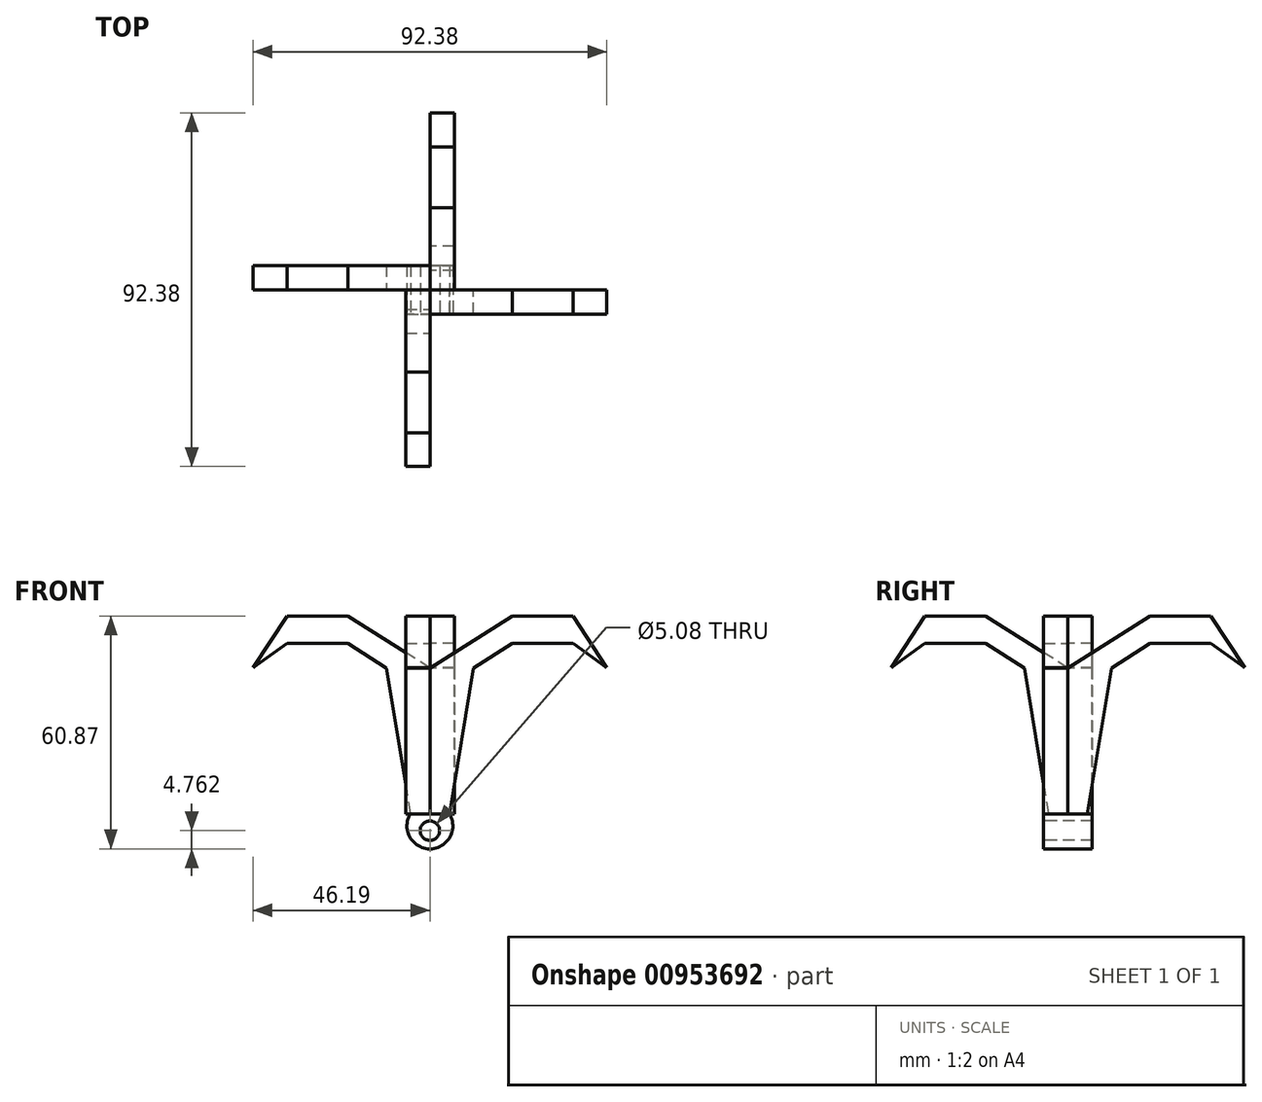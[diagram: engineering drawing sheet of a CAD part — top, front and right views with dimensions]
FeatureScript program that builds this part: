
annotation { "Feature Type Name" : "Feature", "Feature Type Description" : "" }
export const myFeature = defineFeature(function(context is Context, id is Id, definition is map)
    precondition{}
    {
        {
            var Q0;
            Q0=qCreatedBy(makeId("Front.planeOp"),FACE);
            var sketch = newSketch(context, id + "F0", { "sketchPlane" : qUnion([Q0])});
            skLineSegment(sketch, "E0", {"start": v(0, 0) * mm, "end": v(0, 38.1) * mm});
            skLineSegment(sketch, "E1", {"start": v(0, 38.1) * mm, "end": v(21.45, 51.7) * mm});
            skLineSegment(sketch, "E2", {"start": v(21.45, 51.7) * mm, "end": v(37.33, 51.7) * mm});
            skLineSegment(sketch, "E3", {"start": v(37.33, 51.7) * mm, "end": v(46.19, 38.2) * mm});
            skLineSegment(sketch, "E4", {"start": v(46.19, 38.2) * mm, "end": v(37.33, 44.5) * mm});
            skLineSegment(sketch, "E5", {"start": v(37.33, 44.5) * mm, "end": v(21.45, 44.5) * mm});
            skLineSegment(sketch, "E6", {"start": v(21.45, 44.5) * mm, "end": v(11.36, 38.1) * mm});
            skLineSegment(sketch, "E7", {"start": v(11.36, 38.1) * mm, "end": v(5.08, 0) * mm});
            skLineSegment(sketch, "E8", {"start": v(5.08, 0) * mm, "end": v(0, 0) * mm});
            skSolve(sketch);
        }
        {
            var Q0;
            Q0=makeQuery(id+"F0.imprint","IMPRINT",FACE,{"disambiguationData":[TD([[makeQuery(id+"F0.imprint","IMPRINT",EDGE,{"derivedFrom":sQuery(id+"F0.wireOp",EDGE,"E0")}),-1.0]])]});
            extrude(context, id + "F1", {"entities" : qUnion([Q0]), "depth" : 6.35 * mm, "offsetDistance" : 25.4 * mm});
        }
        {
            var Q0;
            Q0=makeQuery(id+"F1.opExtrude","SWEPT_BODY",BODY,{"disambiguationData":[OSD([sQuery(id+"F0.wireOp",EDGE,"E0"),sQuery(id+"F0.wireOp",EDGE,"E1"),sQuery(id+"F0.wireOp",EDGE,"E2"),sQuery(id+"F0.wireOp",EDGE,"E3"),sQuery(id+"F0.wireOp",EDGE,"E4"),sQuery(id+"F0.wireOp",EDGE,"E5"),sQuery(id+"F0.wireOp",EDGE,"E6"),sQuery(id+"F0.wireOp",EDGE,"E7"),sQuery(id+"F0.wireOp",EDGE,"E8")])]});
            var Q1;
            Q1=makeQuery(id+"F1.opExtrude","CAP_EDGE",EDGE,{"disambiguationData":[OSD([sQuery(id+"F0.wireOp",EDGE,"E0")])],"isStart":true});
            circularPattern(context, id + "F2", {"entities" : qUnion([Q0]), "axis" : qUnion([Q1]), "angle" : 360 * degree, "instanceCount" : 4, "equalSpace" : true});
        }
        {
            var Q0;
            Q0=makeQuery(id+"F1.opExtrude","CAP_FACE",FACE,{"disambiguationData":[OSD([sQuery(id+"F0.wireOp",EDGE,"E0"),sQuery(id+"F0.wireOp",EDGE,"E1"),sQuery(id+"F0.wireOp",EDGE,"E2"),sQuery(id+"F0.wireOp",EDGE,"E3"),sQuery(id+"F0.wireOp",EDGE,"E4"),sQuery(id+"F0.wireOp",EDGE,"E5"),sQuery(id+"F0.wireOp",EDGE,"E6"),sQuery(id+"F0.wireOp",EDGE,"E7"),sQuery(id+"F0.wireOp",EDGE,"E8")])],"isStart":false});
            var sketch = newSketch(context, id + "F3", { "sketchPlane" : qUnion([Q0])});
            skLineSegment(sketch, "E9", {"start": v(0, 0) * mm, "end": v(0, -3.18) * mm, "construction": true});
            skArc(sketch, "E10", {"start": v(-5.08, 0) * mm, "mid": v(0, -9.17) * mm, "end": v(5.08, 0) * mm});
            skLineSegment(sketch, "E11", {"start": v(5.08, 0) * mm, "end": v(-5.08, 0) * mm});
            skCircle(sketch, "E12", {"center": v(0, -4.4) * mm, "radius": 2.54 * mm});
            skSolve(sketch);
        }
        {
            var Q0;
            {var subQ0=sQuery(id+"F3.wireOp",EDGE,"E10");Q0=makeQuery(id+"F3.imprint","IMPRINT",FACE,{"disambiguationData":[TD([[makeQuery(id+"F3.imprint","IMPRINT",EDGE,{"derivedFrom":subQ0}),1.0]])]});}
            extrude(context, id + "F4", {"entities" : qUnion([Q0]), "oppositeDirection" : true, "depth" : 12.7 * mm, "offsetDistance" : 25.4 * mm});
        }
    });
